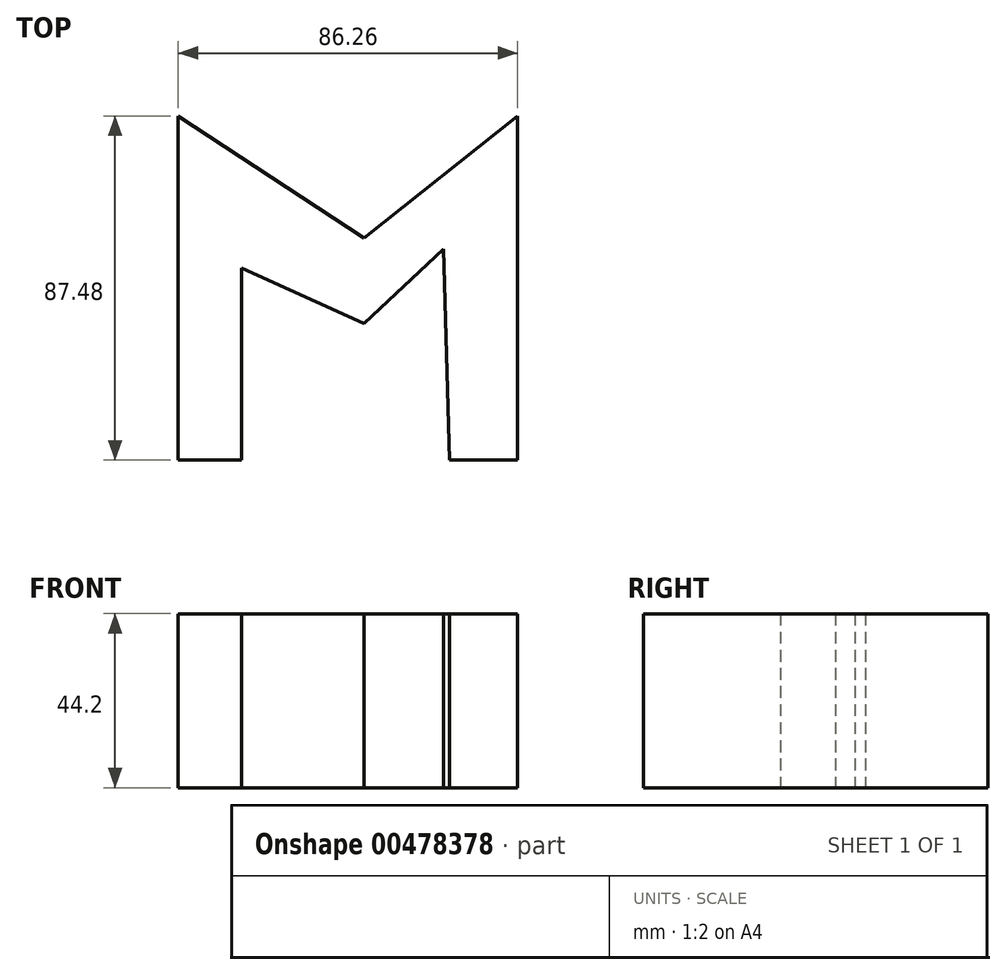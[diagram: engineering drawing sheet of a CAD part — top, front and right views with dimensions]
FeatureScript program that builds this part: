
annotation { "Feature Type Name" : "Feature", "Feature Type Description" : "" }
export const myFeature = defineFeature(function(context is Context, id is Id, definition is map)
    precondition{}
    {
        {
            var Q0;
            Q0=qCreatedBy(makeId("Top.planeOp"),FACE);
            var sketch = newSketch(context, id + "F0", { "sketchPlane" : qUnion([Q0])});
            skLineSegment(sketch, "E0", {"start": v(-50.9, 48.92) * mm, "end": v(-50.9, -38.56) * mm});
            skLineSegment(sketch, "E1", {"start": v(-50.9, -38.56) * mm, "end": v(-34.75, -38.56) * mm});
            skLineSegment(sketch, "E2", {"start": v(-50.9, 48.92) * mm, "end": v(-3.66, 17.83) * mm});
            skLineSegment(sketch, "E3", {"start": v(-3.66, 17.83) * mm, "end": v(35.36, 48.92) * mm});
            skLineSegment(sketch, "E4", {"start": v(35.36, 48.92) * mm, "end": v(35.36, -38.56) * mm});
            skLineSegment(sketch, "E5", {"start": v(35.36, -38.56) * mm, "end": v(17.98, -38.56) * mm});
            skLineSegment(sketch, "E6", {"start": v(-34.75, -38.56) * mm, "end": v(-34.75, 10.21) * mm});
            skLineSegment(sketch, "E7", {"start": v(-34.75, 10.21) * mm, "end": v(-3.66, -3.81) * mm});
            skLineSegment(sketch, "E8", {"start": v(-3.66, -3.81) * mm, "end": v(16.46, 15.09) * mm});
            skLineSegment(sketch, "E9", {"start": v(16.46, 15.09) * mm, "end": v(17.98, -38.56) * mm});
            skSolve(sketch);
        }
        {
            var Q0;
            Q0 = qSketchRegion(id + "F0", true);
            extrude(context, id + "F1", {"entities" : qUnion([Q0]), "depth" : 44.2 * mm});
        }
    });
